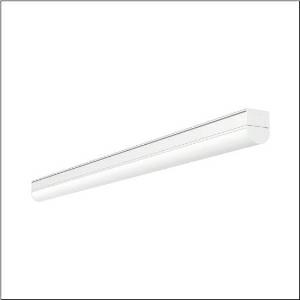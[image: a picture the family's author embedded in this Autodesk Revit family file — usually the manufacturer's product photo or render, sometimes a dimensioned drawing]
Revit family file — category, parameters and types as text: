
# Revit family: ecopack_r__31_51lj12dnm80a_c0ee
name_source: partatom
category: Lighting Fixtures
units: mm (PartAtom-declared; Revit-internal decimal feet)

## family parameters
Cut with Voids When Loaded = No
Host = Face
Light Source = No
Part Type = Normal
Room Calculation Point = No
Round Connector Dimension = Use Diameter
Shared = No

## types (1)
- --- (1 x LED, 6780 lm, 52 W, 5000K)
    Apparent Load = 52 VA
    CIE Flux Codes = 39 67 87 89 100
    Color Rendering = 80
    Color Temperature = 5000K
    Default Elevation = 1800 mm
    Description = Ecopack® 31, diffuser luminaire, primary optical cover: cover, of PC, frosted, light emission: direct distribution, primary light characteristic: symmetric, installation type: surface-mounted, LED, rated luminous flux: 7.000lm, luminous efficacy: 135lm/W, light colour: 830/840/850, colour temperature: 3000/4000/5000K, control gear: DALI 2, with terminal, 5-pole, mains connection: 220..240V, AC, 50/60Hz, rated input power: 52W, housing, of aluminium, traffic white (RAL 9016), length: 1.450mm, width: 56mm, height: 68mm, end cap, of PC, white, protection rating (complete): IP20, insulation class (complete): insulation class I (protective earthing), certification: CE, impact resistance: IK06, permissible operating ambient temperature: -20..+40°C, packaging unit: 1 piece
    Height = 68 mm
    Lamp = 1 x LED
    Lamp Light Flux = 6780 lm
    Lamp Power = 52 W
    Lamp count = 1
    Length = 1450 mm
    Luminous efficacy = 130 lm/W
    Manufacturer = Siteco
    ModVariant = No
    Model = 51LJ12DNM80A
    Mounting Place = Ceiling
    Mounting Type = Surface mounted
    Number of Poles = 1
    OnlyDefault = Yes
    Power Factor = 1
    Product Name = Ecopack® 31
    Product group = diffuser luminaire
    ProductGroupID = 306
    Protection Class = Protection class I
    Protection Degree = IP 20
    RLX_Detail_Level = 1
    RLX_Emergency_Light_Flux = 0 lm
    RLX_Emergency_Type = 0
    RLX_Emergency_Type_DB = No
    RlxData = <blob elided: 21685 chars, md5=8f73be45>
    Socket = socket
    Standby Power = 0 W
    System Light Flux = 6780 lm
    System Power = 52 W
    Type Comments = individual setting: colour temperature 5000K
    Type Image = l_1007033.jpg
    URL = http://relux.com
    VarID = @adj_173944
    Voltage = 0 V
    Weight = 0.00 kg
    Width = 56 mm

## geometry (parser evidence)
native form markers: Blend x4, Sweep x12
no freeform markers — native parametric forms only
